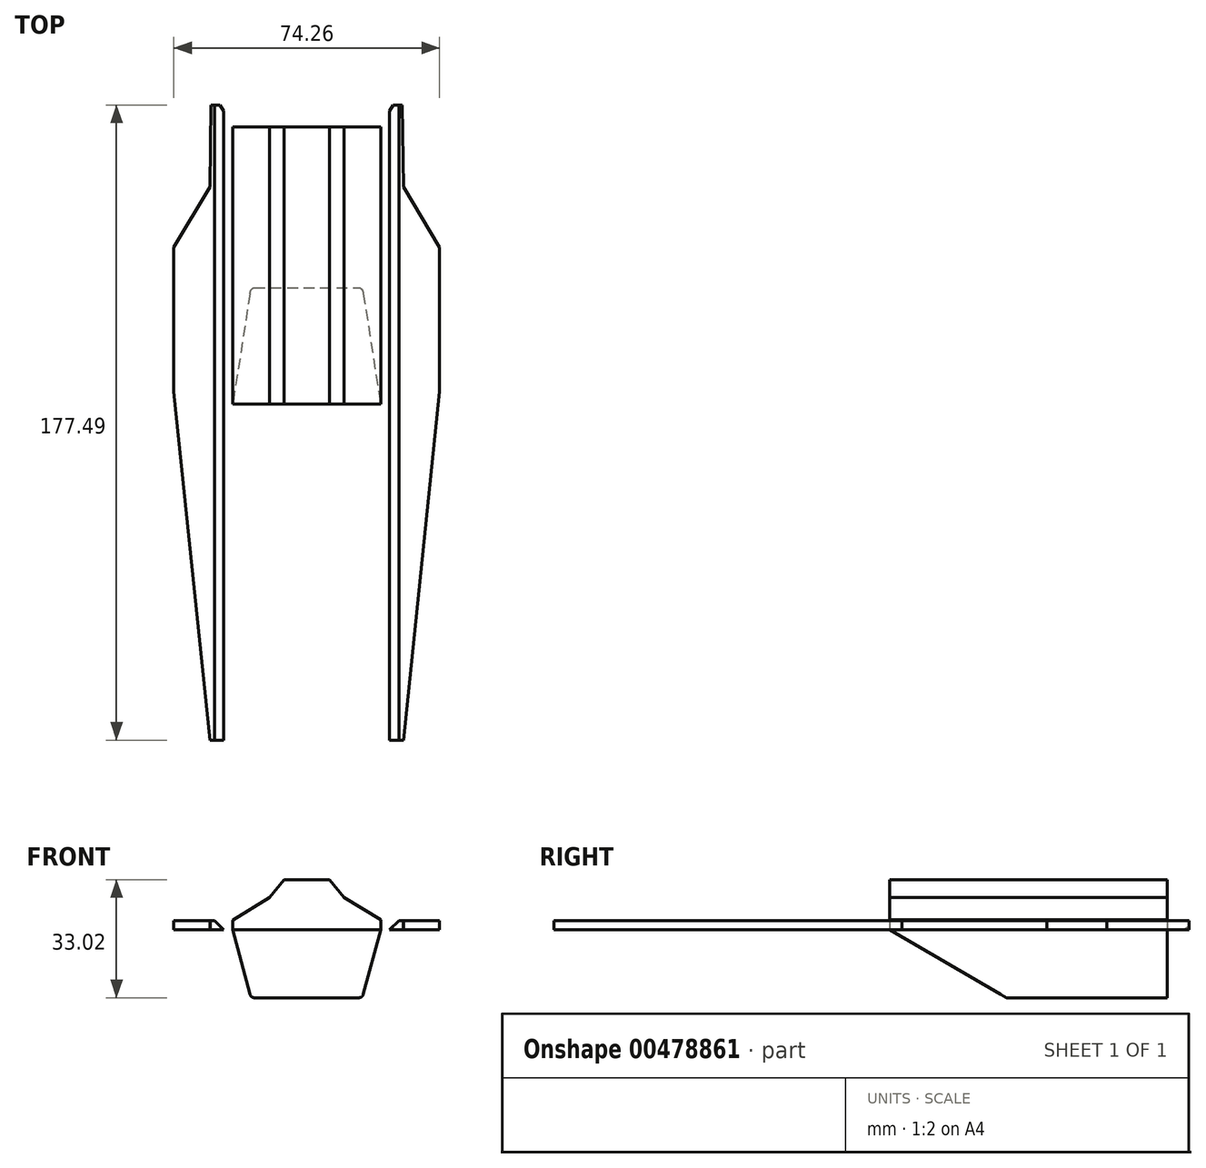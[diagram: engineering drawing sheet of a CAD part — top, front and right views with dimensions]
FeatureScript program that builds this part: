
annotation { "Feature Type Name" : "Feature", "Feature Type Description" : "" }
export const myFeature = defineFeature(function(context is Context, id is Id, definition is map)
    precondition{}
    {
        {
            var Q0;
            Q0=qCreatedBy(makeId("Top.planeOp"),FACE);
            var sketch = newSketch(context, id + "F0", { "sketchPlane" : qUnion([Q0])});
            skLineSegment(sketch, "E0", {"start": v(-27.03, -76.76) * mm, "end": v(-37.13, 20.57) * mm});
            skLineSegment(sketch, "E1", {"start": v(-37.13, 20.57) * mm, "end": v(-37.13, 60.98) * mm});
            skLineSegment(sketch, "E2", {"start": v(-37.13, 60.98) * mm, "end": v(-27.03, 77.83) * mm});
            skLineSegment(sketch, "E3", {"start": v(-27.03, -76.76) * mm, "end": v(-20.68, -76.76) * mm});
            skLineSegment(sketch, "E4", {"start": v(-26.72, 100.73) * mm, "end": v(-24.18, 100.73) * mm});
            skLineSegment(sketch, "E5", {"start": v(-24.18, 100.73) * mm, "end": v(-20.68, 94.69) * mm});
            skLineSegment(sketch, "E6", {"start": v(-20.68, 94.69) * mm, "end": v(-20.68, -76.76) * mm});
            skLineSegment(sketch, "E7", {"start": v(-26.72, 100.73) * mm, "end": v(-27.03, 77.83) * mm});
            skLineSegment(sketch, "E8", {"start": v(0, 46.97) * mm, "end": v(0, -32.3) * mm});
            skLineSegment(sketch, "E9.MirrorCS", {"start": v(26.72, 100.73) * mm, "end": v(24.18, 100.73) * mm});
            skLineSegment(sketch, "E10.MirrorCS", {"start": v(27.03, -76.76) * mm, "end": v(20.68, -76.76) * mm});
            skLineSegment(sketch, "E11.MirrorCS", {"start": v(37.13, 60.98) * mm, "end": v(27.03, 77.83) * mm});
            skLineSegment(sketch, "E12.MirrorCS", {"start": v(37.13, 20.57) * mm, "end": v(37.13, 60.98) * mm});
            skLineSegment(sketch, "E13.MirrorCS", {"start": v(27.03, -76.76) * mm, "end": v(37.13, 20.57) * mm});
            skLineSegment(sketch, "E14.MirrorCS", {"start": v(26.72, 100.73) * mm, "end": v(27.03, 77.83) * mm});
            skLineSegment(sketch, "E15.MirrorCS", {"start": v(24.18, 100.73) * mm, "end": v(20.68, 94.69) * mm});
            skLineSegment(sketch, "E16.MirrorCS", {"start": v(20.68, 94.69) * mm, "end": v(20.68, -76.76) * mm});
            skSolve(sketch);
        }
        {
            var Q0;
            Q0=qSketchRegion(id+"F0",true);
            extrude(context, id + "F1", {"entities" : qUnion([Q0]), "depth" : 2.54 * mm});
        }
        {
            var Q0;
            Q0=qCreatedBy(makeId("Top.planeOp"),FACE);
            var sketch = newSketch(context, id + "F2", { "sketchPlane" : qUnion([Q0])});
            skPoint(sketch, "E17.0", {"position": v(-20.68, 94.69) * mm});
            skPoint(sketch, "E18.0", {"position": v(20.68, 94.69) * mm});
            skLineSegment(sketch, "E19.bottom", {"start": v(-20.68, 94.69) * mm, "end": v(20.68, 94.69) * mm});
            skLineSegment(sketch, "E19.top", {"start": v(-20.68, 17.14) * mm, "end": v(20.68, 17.14) * mm});
            skLineSegment(sketch, "E19.left", {"start": v(-20.68, 94.69) * mm, "end": v(-20.68, 17.14) * mm});
            skLineSegment(sketch, "E19.right", {"start": v(20.68, 94.69) * mm, "end": v(20.68, 17.14) * mm});
            skSolve(sketch);
        }
        {
            var Q0;
            Q0=qSketchRegion(id+"F2",true);
            extrude(context, id + "F3", {"entities" : qUnion([Q0]), "endBound" : BoundingType.SYMMETRIC, "depth" : 38.1 * mm});
        }
        {
            var Q0;
            Q0=makeQuery(id+"F3.opExtrude","SWEPT_FACE",FACE,{"disambiguationData":[OSD([sQuery(id+"F2.wireOp",EDGE,"E19.right")])]});
            var sketch = newSketch(context, id + "F4", { "sketchPlane" : qUnion([Q0])});
            skLineSegment(sketch, "E20", {"start": v(17.14, 0) * mm, "end": v(49.7, -19.05) * mm});
            skLineSegment(sketch, "E21", {"start": v(49.7, -19.05) * mm, "end": v(17.14, -19.05) * mm});
            skLineSegment(sketch, "E22", {"start": v(17.14, -19.05) * mm, "end": v(17.14, 0) * mm});
            skSolve(sketch);
        }
        {
            var Q0;
            Q0=qSketchRegion(id+"F4",true);
            extrude(context, id + "F5", {"entities" : qUnion([Q0]), "operationType" : NewBodyOperationType.REMOVE, "oppositeDirection" : true, "depth" : 41.66 * mm});
        }
        {
            var Q0;
            Q0=makeQuery(id+"F3.opExtrude","CAP_EDGE",EDGE,{"disambiguationData":[OSD([sQuery(id+"F2.wireOp",EDGE,"E19.right")])],"isStart":true});
            var Q1;
            Q1=makeQuery(id+"F3.opExtrude","CAP_EDGE",EDGE,{"disambiguationData":[OSD([sQuery(id+"F2.wireOp",EDGE,"E19.left")])],"isStart":true});
            chamfer(context, id + "F6", {"entities" : qUnion([Q0, Q1]), "chamferType" : ChamferType.TWO_OFFSETS, "width1" : 5.08 * mm, "oppositeDirection" : false, "width2" : 19.05 * mm, "tangentPropagation" : true});
        }
        {
            var Q0;
            {var subQ0=sQuery(id+"F2.wireOp",EDGE,"E19.right");Q0=makeQuery(id+"F6.opChamfer","BLEND_EDGE",EDGE,{"blendedFrom":[makeQuery(id+"F3.opExtrude","CAP_EDGE",EDGE,{"disambiguationData":[OSD([subQ0])],"isStart":true}),makeQuery(id+"F3.opExtrude","CAP_FACE",FACE,{"disambiguationData":[OSD([sQuery(id+"F2.wireOp",EDGE,"E19.bottom"),sQuery(id+"F2.wireOp",EDGE,"E19.top"),sQuery(id+"F2.wireOp",EDGE,"E19.left"),subQ0])],"isStart":true})],"blendedInto":[makeQuery(id+"F3.opExtrude","CAP_FACE",FACE,{"disambiguationData":[OSD([sQuery(id+"F2.wireOp",EDGE,"E19.bottom"),sQuery(id+"F2.wireOp",EDGE,"E19.top"),sQuery(id+"F2.wireOp",EDGE,"E19.left"),subQ0])],"isStart":true})]});}
            var Q1;
            {var subQ0=sQuery(id+"F2.wireOp",EDGE,"E19.left");Q1=makeQuery(id+"F6.opChamfer","BLEND_EDGE",EDGE,{"blendedFrom":[makeQuery(id+"F3.opExtrude","CAP_EDGE",EDGE,{"disambiguationData":[OSD([subQ0])],"isStart":true}),makeQuery(id+"F3.opExtrude","CAP_FACE",FACE,{"disambiguationData":[OSD([sQuery(id+"F2.wireOp",EDGE,"E19.bottom"),sQuery(id+"F2.wireOp",EDGE,"E19.top"),subQ0,sQuery(id+"F2.wireOp",EDGE,"E19.right")])],"isStart":true})],"blendedInto":[makeQuery(id+"F3.opExtrude","CAP_FACE",FACE,{"disambiguationData":[OSD([sQuery(id+"F2.wireOp",EDGE,"E19.bottom"),sQuery(id+"F2.wireOp",EDGE,"E19.top"),subQ0,sQuery(id+"F2.wireOp",EDGE,"E19.right")])],"isStart":true})]});}
            fillet(context, id + "F7", {"entities" : qUnion([Q0, Q1]), "radius" : 1.27 * mm, "tangentPropagation" : true, "allowEdgeOverflow" : false});
        }
        {
            var Q0;
            Q0=makeQuery(id+"F3.opExtrude","SWEPT_FACE",FACE,{"disambiguationData":[OSD([sQuery(id+"F2.wireOp",EDGE,"E19.top")])]});
            var sketch = newSketch(context, id + "F8", { "sketchPlane" : qUnion([Q0])});
            skLineSegment(sketch, "E23", {"start": v(-20.68, 2.64) * mm, "end": v(-10.42, 8.97) * mm});
            skLineSegment(sketch, "E24", {"start": v(-10.42, 8.97) * mm, "end": v(-6.35, 13.97) * mm});
            skLineSegment(sketch, "E25", {"start": v(-6.35, 13.97) * mm, "end": v(6.35, 13.97) * mm});
            skLineSegment(sketch, "E26", {"start": v(6.35, 13.97) * mm, "end": v(10.41, 8.97) * mm});
            skLineSegment(sketch, "E27", {"start": v(10.41, 8.97) * mm, "end": v(20.68, 2.76) * mm});
            skLineSegment(sketch, "E28", {"start": v(-20.68, 2.64) * mm, "end": v(-20.68, 19.05) * mm});
            skLineSegment(sketch, "E29", {"start": v(-20.68, 19.05) * mm, "end": v(20.68, 19.05) * mm});
            skLineSegment(sketch, "E30", {"start": v(20.68, 19.05) * mm, "end": v(20.68, 2.76) * mm});
            skSolve(sketch);
        }
        {
            var Q0;
            Q0=qSketchRegion(id+"F8",true);
            extrude(context, id + "F9", {"entities" : qUnion([Q0]), "operationType" : NewBodyOperationType.REMOVE, "endBound" : BoundingType.THROUGH_ALL, "oppositeDirection" : true, "depth" : 25.4 * mm});
        }
        {
            var Q0;
            Q0=makeQuery(id+"F1.opExtrude","CAP_EDGE",EDGE,{"disambiguationData":[OSD([sQuery(id+"F0.wireOp",EDGE,"E16.MirrorCS")])],"isStart":false});
            var Q1;
            Q1=makeQuery(id+"F1.opExtrude","CAP_EDGE",EDGE,{"disambiguationData":[OSD([sQuery(id+"F0.wireOp",EDGE,"E6")])],"isStart":false});
            chamfer(context, id + "F10", {"entities" : qUnion([Q0, Q1]), "width" : 5.08 * mm, "tangentPropagation" : true});
        }
    });
